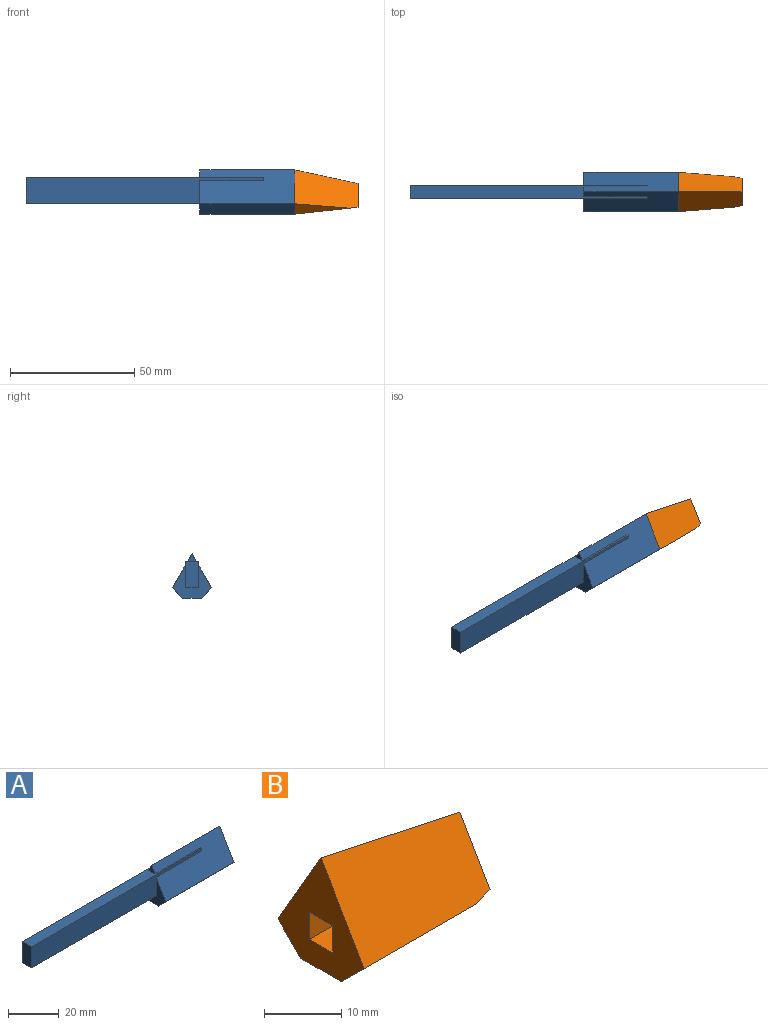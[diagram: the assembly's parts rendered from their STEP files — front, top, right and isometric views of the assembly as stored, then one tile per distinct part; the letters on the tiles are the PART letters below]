
ASSEMBLY  parts=2 mates=1
PART A: 20 faces, bbox 108x15.7x17.8 mm
  f0: plane 17.78x15.74mm, normal (1,0,0), area 136.7mm2, adj f1,f2,f12,f13,f14,f15,f16,f17
  f1: plane 38.1x13.63mm, normal (0,-0.87,0.5), area 563.7mm2, adj f0,f2,f3,f4,f6,f7,f11,f13
  f2: plane 38.1x13.63mm, normal (0,0.87,0.5), area 563.7mm2, adj f0,f1,f3,f4,f7,f8,f10,f14
  f3: plane 3.67x3.18mm, normal (-1,0,0), area 5.8mm2, adj f1,f2,f7
  f4: plane 15.74x13.38mm, normal (-1,0,0), area 98.8mm2, adj f1,f2,f5,f6,f8,f12,f13,f14
  f5: plane 69.85x5.08mm, normal (0,0,-1), area 354.8mm2, adj f4,f6,f8,f9
  f6: plane 95.25x10.16mm, normal (0,-1,0), area 740.8mm2, adj f1,f4,f5,f7,f9,f11
  f7: plane 95.25x5.08mm, normal (0,0,1), area 390.7mm2, adj f1,f2,f3,f6,f8,f9,f10,f11
  f8: plane 95.25x10.16mm, normal (0,1,0), area 740.8mm2, adj f2,f4,f5,f7,f9,f10
  f9: plane 10.16x5.08mm, normal (-1,0,0), area 51.6mm2, adj f5,f6,f7,f8
  f10: plane 1.22x0.71mm, normal (1,0,0), area 0.4mm2, adj f2,f7,f8
  f11: plane 1.22x0.71mm, normal (1,0,0), area 0.4mm2, adj f1,f6,f7
  f12: plane 38.1x7.44mm, normal (0,0,-1), area 283.4mm2, adj f0,f4,f13,f14
  f13: plane 38.1x4.15mm, normal (0,-0.71,-0.71), area 223.6mm2, adj f0,f1,f4,f12
  f14: plane 38.1x4.15mm, normal (0,0.71,-0.71), area 223.6mm2, adj f0,f2,f4,f12
  f15: plane 25.4x4.32mm, normal (0,-1,0), area 109.7mm2, adj f0,f16,f18,f19
  f16: plane 25.4x4.32mm, normal (0,0,-1), area 109.7mm2, adj f0,f15,f17,f19
  f17: plane 25.4x4.32mm, normal (0,1,0), area 109.7mm2, adj f0,f16,f18,f19
  f18: plane 25.4x4.32mm, normal (0,0,1), area 109.7mm2, adj f0,f15,f17,f19
  f19: plane 4.32x4.32mm, normal (1,0,0), area 18.6mm2, adj f15,f16,f17,f18
PART B: 11 faces, bbox 25.4x15.7x17.8 mm
  f0: plane 17.78x15.74mm, normal (-1,0,0), area 136.7mm2, adj f2,f3,f4,f5,f6,f7,f8,f9
  f1: plane 11x9.53mm, normal (1,0,0), area 33.7mm2, adj f2,f3,f4,f7,f8,f9,f10
  f2: plane 25.4x15.38mm, normal (0.11,-0.86,0.5), area 349.5mm2, adj f0,f1,f3,f4,f5
  f3: plane 25.4x12.23mm, normal (0.11,0,-0.99), area 257.1mm2, adj f0,f1,f2,f4,f5,f6
  f4: plane 25.4x15.38mm, normal (0.11,0.86,0.5), area 349.5mm2, adj f0,f1,f2,f3,f6
  f5: plane 22.12x4.15mm, normal (0,-0.71,-0.71), area 64.9mm2, adj f0,f2,f3
  f6: plane 22.12x4.15mm, normal (0,0.71,-0.71), area 64.9mm2, adj f0,f3,f4
  f7: plane 25.4x4.32mm, normal (0,0,1), area 109.7mm2, adj f0,f1,f8,f10
  f8: plane 25.4x4.32mm, normal (0,-1,0), area 109.7mm2, adj f0,f1,f7,f9
  f9: plane 25.4x4.32mm, normal (0,0,-1), area 109.7mm2, adj f0,f1,f8,f10
  f10: plane 25.4x4.32mm, normal (0,1,0), area 109.7mm2, adj f0,f1,f7,f9
PLACE A t=(-33.13,19.35,12.42)mm
PLACE B t=(4.97,19.35,10.72)mm
MATE fastened A.f0 <-> B.f0  axis (1,0,0) through (4.97,19.35,11.63)mm
